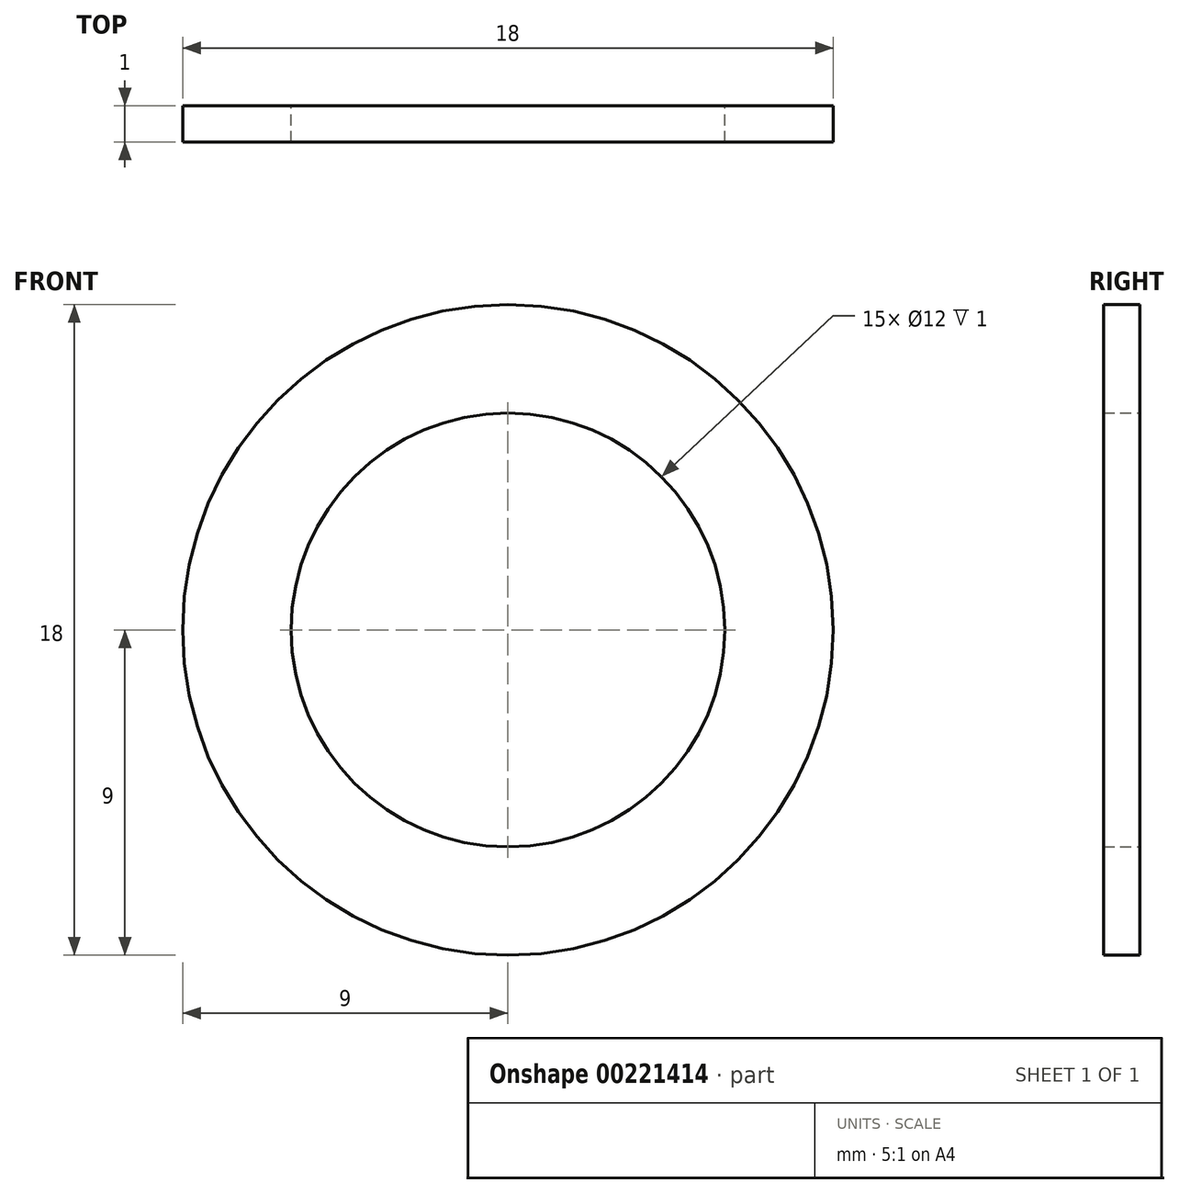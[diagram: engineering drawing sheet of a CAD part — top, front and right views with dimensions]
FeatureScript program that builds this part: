
annotation { "Feature Type Name" : "Feature", "Feature Type Description" : "" }
export const myFeature = defineFeature(function(context is Context, id is Id, definition is map)
    precondition{}
    {
        {
            var Q0;
            Q0=qCreatedBy(makeId("Front.planeOp"),FACE);
            var sketch = newSketch(context, id + "F0", { "sketchPlane" : qUnion([Q0])});
            skCircle(sketch, "E0", {"center": v(0, 0) * mm, "radius": 6 * mm});
            skCircle(sketch, "E1", {"center": v(0, 0) * mm, "radius": 9 * mm});
            skSolve(sketch);
        }
        {
            var Q0;
            Q0 = qSketchRegion(id + "F0", true);
            extrude(context, id + "F1", {"entities" : qUnion([Q0]), "depth" : 1 * mm});
        }
    });
